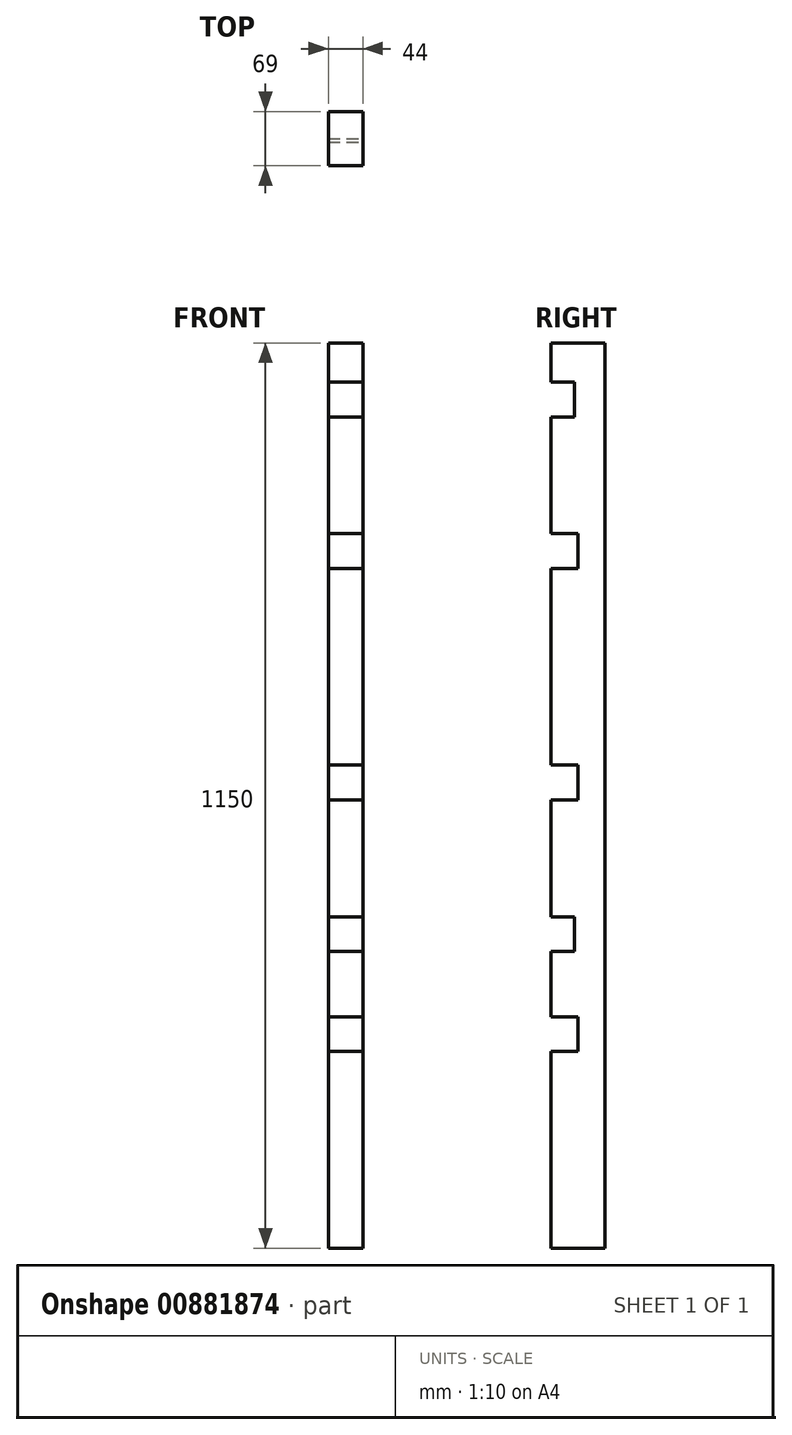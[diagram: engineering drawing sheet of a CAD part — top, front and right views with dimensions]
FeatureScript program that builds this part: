
annotation { "Feature Type Name" : "Feature", "Feature Type Description" : "" }
export const myFeature = defineFeature(function(context is Context, id is Id, definition is map)
    precondition{}
    {
        {
            var Q0;
            Q0=qCreatedBy(makeId("Top.planeOp"),FACE);
            var sketch = newSketch(context, id + "F0", { "sketchPlane" : qUnion([Q0])});
            skLineSegment(sketch, "E0.bottom", {"start": v(22, -34.5) * mm, "end": v(-22, -34.5) * mm});
            skLineSegment(sketch, "E0.top", {"start": v(22, 34.5) * mm, "end": v(-22, 34.5) * mm});
            skLineSegment(sketch, "E0.left", {"start": v(22, -34.5) * mm, "end": v(22, 34.5) * mm});
            skLineSegment(sketch, "E0.right", {"start": v(-22, -34.5) * mm, "end": v(-22, 34.5) * mm});
            skPoint(sketch, "E0.middle", {"position": v(0, 0) * mm});
            skSolve(sketch);
        }
        {
            var Q0;
            Q0=qSketchRegion(id+"F0",true);
            extrude(context, id + "F1", {"entities" : qUnion([Q0]), "depth" : 1100 * mm, "offsetDistance" : 25 * mm});
        }
        {
            var Q0;
            Q0=makeQuery(id+"F1.opExtrude","SWEPT_FACE",FACE,{"disambiguationData":[OSD([sQuery(id+"F0.wireOp",EDGE,"E0.left")])]});
            var sketch = newSketch(context, id + "F2", { "sketchPlane" : qUnion([Q0])});
            skLineSegment(sketch, "E1", {"start": v(-34.5, 1050) * mm, "end": v(-4.5, 1050) * mm});
            skLineSegment(sketch, "E2", {"start": v(-4.5, 1050) * mm, "end": v(-4.5, 1006) * mm});
            skLineSegment(sketch, "E3", {"start": v(-4.5, 1006) * mm, "end": v(-34.5, 1006) * mm});
            skLineSegment(sketch, "E4", {"start": v(-34.5, 1050) * mm, "end": v(-34.5, 1006) * mm});
            skLineSegment(sketch, "E5", {"start": v(-34.5, 371) * mm, "end": v(-4.5, 371) * mm});
            skLineSegment(sketch, "E6", {"start": v(-4.5, 371) * mm, "end": v(-4.5, 327) * mm});
            skLineSegment(sketch, "E7", {"start": v(-4.5, 327) * mm, "end": v(-34.5, 327) * mm});
            skLineSegment(sketch, "E8", {"start": v(-34.5, 327) * mm, "end": v(-34.5, 371) * mm});
            skSolve(sketch);
        }
        {
            var Q0;
            Q0=qSketchRegion(id+"F2",true);
            extrude(context, id + "F3", {"entities" : qUnion([Q0]), "operationType" : NewBodyOperationType.REMOVE, "endBound" : BoundingType.THROUGH_ALL, "oppositeDirection" : true, "depth" : 25 * mm, "offsetDistance" : 25 * mm});
        }
        {
            var Q0;
            Q0=makeQuery(id+"F1.opExtrude","SWEPT_FACE",FACE,{"disambiguationData":[OSD([sQuery(id+"F0.wireOp",EDGE,"E0.left")])]});
            var sketch = newSketch(context, id + "F4", { "sketchPlane" : qUnion([Q0])});
            skLineSegment(sketch, "E9", {"start": v(-34.5, 688.5) * mm, "end": v(34.5, 688.5) * mm, "construction": true});
            skLineSegment(sketch, "E10", {"start": v(-34.5, 813.5) * mm, "end": v(0, 813.5) * mm});
            skLineSegment(sketch, "E11", {"start": v(-34.5, 857.5) * mm, "end": v(0, 857.5) * mm});
            skLineSegment(sketch, "E12", {"start": v(0, 857.5) * mm, "end": v(0, 813.5) * mm});
            skLineSegment(sketch, "E13", {"start": v(-34.5, 857.5) * mm, "end": v(-34.5, 813.5) * mm});
            skLineSegment(sketch, "E14.MirrorCS", {"start": v(-34.5, 563.5) * mm, "end": v(0, 563.5) * mm});
            skLineSegment(sketch, "E15.MirrorCS", {"start": v(-34.5, 519.5) * mm, "end": v(-34.5, 563.5) * mm});
            skLineSegment(sketch, "E16.MirrorCS", {"start": v(-34.5, 519.5) * mm, "end": v(0, 519.5) * mm});
            skLineSegment(sketch, "E17.MirrorCS", {"start": v(0, 519.5) * mm, "end": v(0, 563.5) * mm});
            skSolve(sketch);
        }
        {
            var Q0;
            Q0=qSketchRegion(id+"F4",true);
            extrude(context, id + "F5", {"entities" : qUnion([Q0]), "operationType" : NewBodyOperationType.REMOVE, "endBound" : BoundingType.THROUGH_ALL, "oppositeDirection" : true, "depth" : 25 * mm, "offsetDistance" : 25 * mm});
        }
        {
            var Q0;
            Q0=makeQuery(id+"F1.opExtrude","CAP_FACE",FACE,{"disambiguationData":[OSD([sQuery(id+"F0.wireOp",EDGE,"E0.bottom"),sQuery(id+"F0.wireOp",EDGE,"E0.top"),sQuery(id+"F0.wireOp",EDGE,"E0.left"),sQuery(id+"F0.wireOp",EDGE,"E0.right")])],"isStart":true});
            extrude(context, id + "F6", {"entities" : qUnion([Q0]), "operationType" : NewBodyOperationType.ADD, "depth" : 50 * mm, "offsetDistance" : 25 * mm});
        }
        {
            var Q0;
            {var subQ0=sQuery(id+"F0.wireOp",EDGE,"E0.left");Q0=makeQuery(id+"F6.boolean.opBoolean","MERGE",FACE,{"derivedFrom":[makeQuery(id+"F1.opExtrude","SWEPT_FACE",FACE,{"disambiguationData":[OSD([subQ0])]}),makeQuery(id+"F6.opExtrude","SWEPT_FACE",FACE,{"disambiguationData":[OSD([subQ0])]})]});}
            var sketch = newSketch(context, id + "F7", { "sketchPlane" : qUnion([Q0])});
            skLineSegment(sketch, "E18", {"start": v(-34.5, 200) * mm, "end": v(0, 200) * mm});
            skLineSegment(sketch, "E19", {"start": v(0, 200) * mm, "end": v(0, 244) * mm});
            skLineSegment(sketch, "E20", {"start": v(0, 244) * mm, "end": v(-34.5, 244) * mm});
            skLineSegment(sketch, "E21", {"start": v(-34.5, 244) * mm, "end": v(-34.5, 200) * mm});
            skSolve(sketch);
        }
        {
            var Q0;
            Q0=makeQuery(id+"F7.imprint","IMPRINT",FACE,{"disambiguationData":[TD([[makeQuery(id+"F7.imprint","IMPRINT",EDGE,{"derivedFrom":sQuery(id+"F7.wireOp",EDGE,"E18")}),1.0]])]});
            extrude(context, id + "F8", {"entities" : qUnion([Q0]), "operationType" : NewBodyOperationType.REMOVE, "oppositeDirection" : true, "depth" : 133 * mm, "offsetDistance" : 25 * mm});
        }
    });
